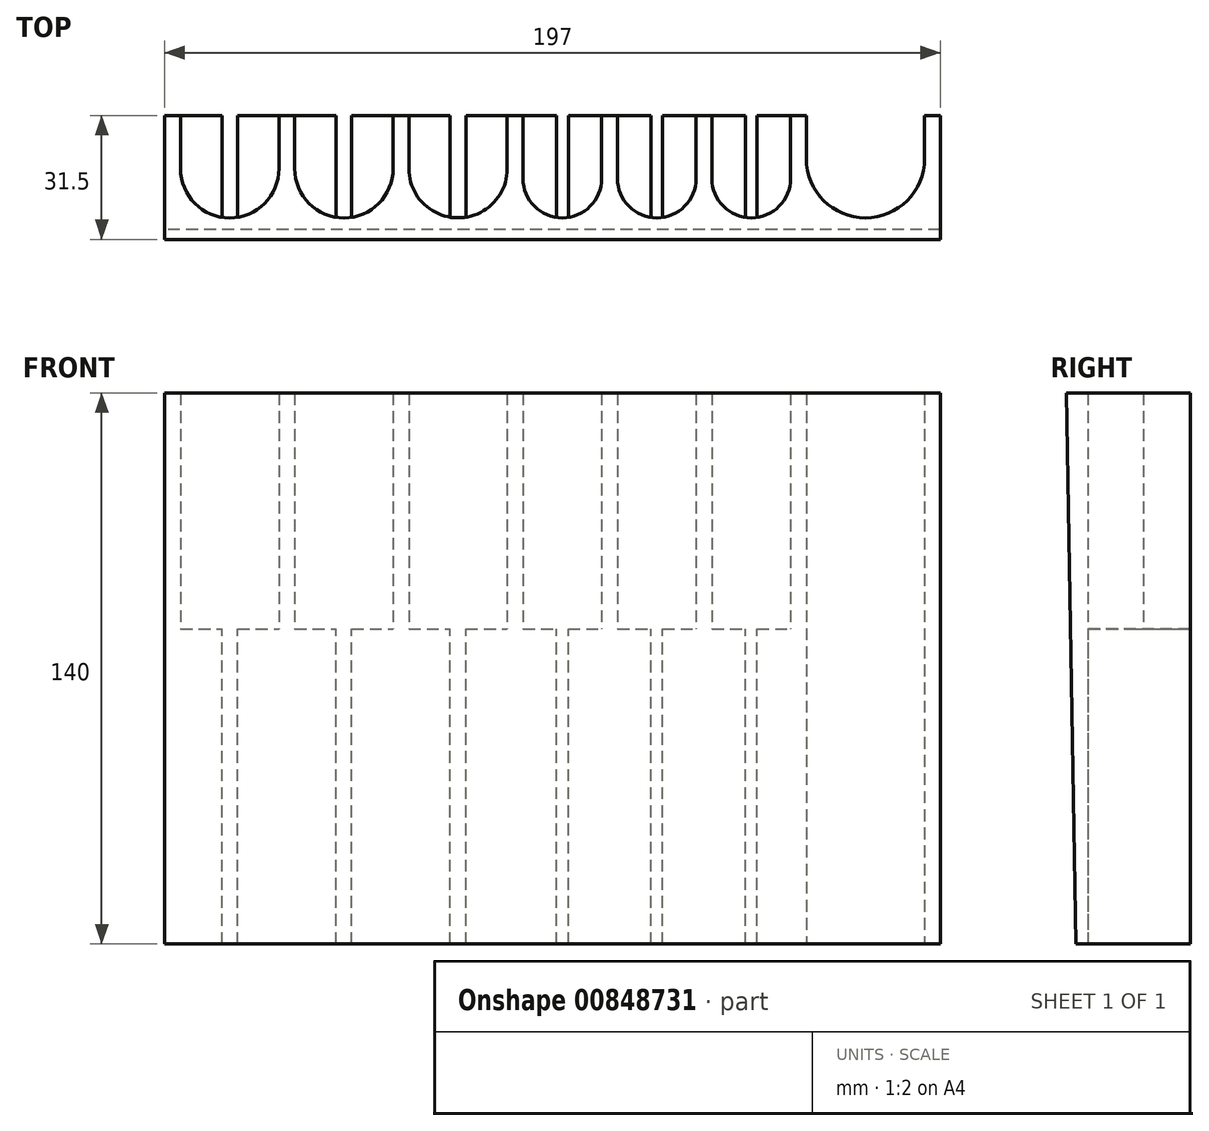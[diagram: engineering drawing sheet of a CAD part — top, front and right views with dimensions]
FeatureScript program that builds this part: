
annotation { "Feature Type Name" : "Feature", "Feature Type Description" : "" }
export const myFeature = defineFeature(function(context is Context, id is Id, definition is map)
    precondition{}
    {
        {
            var Q0;
            Q0=qCreatedBy(makeId("Top.planeOp"),FACE);
            var sketch = newSketch(context, id + "F0", { "sketchPlane" : qUnion([Q0])});
            skLineSegment(sketch, "E0.bottom", {"start": v(-180, 30) * mm, "end": v(0, 30) * mm});
            skLineSegment(sketch, "E0.top", {"start": v(-180, 0) * mm, "end": v(0, 0) * mm});
            skLineSegment(sketch, "E0.left", {"start": v(-180, 30) * mm, "end": v(-180, 0) * mm});
            skArc(sketch, "E1", {"start": v(-176, 16.5) * mm, "mid": v(-163.5, 4) * mm, "end": v(-151, 16.5) * mm});
            skArc(sketch, "E2", {"start": v(-147, 16.5) * mm, "mid": v(-134.5, 4) * mm, "end": v(-122, 16.5) * mm});
            skArc(sketch, "E3", {"start": v(-118, 16.5) * mm, "mid": v(-104.7, 4.03) * mm, "end": v(-93.1, 18.1) * mm});
            skArc(sketch, "E4", {"start": v(-89, 14) * mm, "mid": v(-79, 4) * mm, "end": v(-69, 14) * mm});
            skArc(sketch, "E5", {"start": v(-65, 14) * mm, "mid": v(-55, 4) * mm, "end": v(-45, 14) * mm});
            skArc(sketch, "E6", {"start": v(-41, 14) * mm, "mid": v(-31, 4) * mm, "end": v(-21, 14) * mm});
            skLineSegment(sketch, "E7.bottom", {"start": v(0, 30) * mm, "end": v(17, 30) * mm});
            skLineSegment(sketch, "E7.top", {"start": v(0, 0) * mm, "end": v(17, 0) * mm});
            skArc(sketch, "E8", {"start": v(-17, 19) * mm, "mid": v(-2, 4) * mm, "end": v(13, 19) * mm});
            skLineSegment(sketch, "E9", {"start": v(-176, 16.5) * mm, "end": v(-176, 30) * mm});
            skLineSegment(sketch, "E10", {"start": v(-151, 16.5) * mm, "end": v(-151, 30) * mm});
            skLineSegment(sketch, "E11", {"start": v(-147, 16.5) * mm, "end": v(-147, 30) * mm});
            skLineSegment(sketch, "E12", {"start": v(-122, 16.5) * mm, "end": v(-122, 30) * mm});
            skLineSegment(sketch, "E13", {"start": v(-118, 16.5) * mm, "end": v(-118, 30) * mm});
            skLineSegment(sketch, "E14", {"start": v(-93.1, 18.1) * mm, "end": v(-93.1, 30) * mm});
            skLineSegment(sketch, "E15", {"start": v(-89, 14) * mm, "end": v(-89, 30) * mm});
            skLineSegment(sketch, "E16", {"start": v(-69, 14) * mm, "end": v(-69, 30) * mm});
            skLineSegment(sketch, "E17", {"start": v(-65, 14) * mm, "end": v(-65, 30) * mm});
            skLineSegment(sketch, "E18", {"start": v(-45, 14) * mm, "end": v(-45, 30) * mm});
            skLineSegment(sketch, "E19", {"start": v(-41, 14) * mm, "end": v(-41, 30) * mm});
            skLineSegment(sketch, "E20", {"start": v(-21, 14) * mm, "end": v(-21, 30) * mm});
            skLineSegment(sketch, "E21", {"start": v(-17, 19) * mm, "end": v(-17, 30) * mm});
            skLineSegment(sketch, "E22", {"start": v(13, 19) * mm, "end": v(13, 30) * mm});
            skLineSegment(sketch, "E23", {"start": v(-56.5, 30) * mm, "end": v(-56.5, 10.18) * mm});
            skLineSegment(sketch, "E24", {"start": v(-53.5, 30) * mm, "end": v(-53.5, 10.01) * mm});
            skLineSegment(sketch, "E25", {"start": v(-32.5, 30) * mm, "end": v(-32.5, 17.37) * mm});
            skLineSegment(sketch, "E26", {"start": v(-29.5, 30) * mm, "end": v(-29.5, 17.22) * mm});
            skLineSegment(sketch, "E27", {"start": v(-80.5, 30) * mm, "end": v(-80.5, 18.02) * mm});
            skLineSegment(sketch, "E28", {"start": v(-77.5, 30) * mm, "end": v(-77.5, 17.52) * mm});
            skLineSegment(sketch, "E29", {"start": v(-132.5, 30) * mm, "end": v(-132.5, 14.05) * mm});
            skLineSegment(sketch, "E30", {"start": v(-136.5, 30) * mm, "end": v(-136.5, 13.27) * mm});
            skLineSegment(sketch, "E31", {"start": v(-161.5, 30) * mm, "end": v(-161.5, 11.13) * mm});
            skLineSegment(sketch, "E32", {"start": v(-165.5, 30) * mm, "end": v(-165.5, 8.65) * mm});
            skLineSegment(sketch, "E33", {"start": v(-107.5, 30) * mm, "end": v(-107.5, 11.19) * mm});
            skLineSegment(sketch, "E34", {"start": v(-103.5, 30) * mm, "end": v(-103.5, 10.64) * mm});
            skLineSegment(sketch, "E35", {"start": v(-165.5, 8.65) * mm, "end": v(-165.5, 4.16) * mm});
            skLineSegment(sketch, "E36", {"start": v(-161.5, 11.13) * mm, "end": v(-161.5, 4.16) * mm});
            skLineSegment(sketch, "E37", {"start": v(-136.5, 13.27) * mm, "end": v(-136.5, 4.16) * mm});
            skLineSegment(sketch, "E38", {"start": v(-132.5, 14.05) * mm, "end": v(-132.5, 4.16) * mm});
            skLineSegment(sketch, "E39", {"start": v(-107.5, 11.19) * mm, "end": v(-107.5, 4.16) * mm});
            skLineSegment(sketch, "E40", {"start": v(-103.5, 10.64) * mm, "end": v(-103.5, 4.16) * mm});
            skLineSegment(sketch, "E41", {"start": v(-80.5, 18.02) * mm, "end": v(-80.5, 4.11) * mm});
            skLineSegment(sketch, "E42", {"start": v(-77.5, 17.52) * mm, "end": v(-77.5, 4.11) * mm});
            skLineSegment(sketch, "E43", {"start": v(-56.5, 10.18) * mm, "end": v(-56.5, 4.11) * mm});
            skLineSegment(sketch, "E44", {"start": v(-53.5, 10.01) * mm, "end": v(-53.5, 4.11) * mm});
            skLineSegment(sketch, "E45", {"start": v(-32.5, 17.37) * mm, "end": v(-32.5, 4.11) * mm});
            skLineSegment(sketch, "E46", {"start": v(-29.5, 17.22) * mm, "end": v(-29.5, 4.11) * mm});
            skLineSegment(sketch, "E47", {"start": v(17, 30) * mm, "end": v(17, 0) * mm});
            skPoint(sketch, "E48.orphan", {"position": v(20, 0) * mm});
            skSolve(sketch);
        }
        {
            var Q0;
            Q0=makeQuery(id+"F0.imprint","IMPRINT",FACE,{"disambiguationData":[TD([[makeQuery(id+"F0.imprint","IMPRINT",EDGE,{"derivedFrom":sQuery(id+"F0.wireOp",EDGE,"E0.top")}),1.0]])]});
            extrude(context, id + "F1", {"entities" : qUnion([Q0]), "depth" : 60 * mm, "offsetDistance" : 25 * mm});
        }
        {
            var Q0;
            Q0=makeQuery(id+"F0.imprint","IMPRINT",FACE,{"disambiguationData":[TD([[makeQuery(id+"F0.imprint","IMPRINT",EDGE,{"derivedFrom":sQuery(id+"F0.wireOp",EDGE,"E0.top")}),1.0]])]});
            var Q1;
            {var subQ1=sQuery(id+"F0.wireOp",EDGE,"E9");Q1=makeQuery(id+"F0.imprint","IMPRINT",FACE,{"disambiguationData":[TD([[makeQuery(id+"F0.imprint","IMPRINT",EDGE,{"derivedFrom":subQ1}),-1.0]])]});}
            var Q2;
            {var subQ0=sQuery(id+"F0.wireOp",EDGE,"E10");Q2=makeQuery(id+"F0.imprint","IMPRINT",FACE,{"disambiguationData":[TD([[makeQuery(id+"F0.imprint","IMPRINT",EDGE,{"derivedFrom":subQ0}),1.0]])]});}
            var Q3;
            {var subQ1=sQuery(id+"F0.wireOp",EDGE,"E11");Q3=makeQuery(id+"F0.imprint","IMPRINT",FACE,{"disambiguationData":[TD([[makeQuery(id+"F0.imprint","IMPRINT",EDGE,{"derivedFrom":subQ1}),-1.0]])]});}
            var Q4;
            {var subQ1=sQuery(id+"F0.wireOp",EDGE,"E12");Q4=makeQuery(id+"F0.imprint","IMPRINT",FACE,{"disambiguationData":[TD([[makeQuery(id+"F0.imprint","IMPRINT",EDGE,{"derivedFrom":subQ1}),1.0]])]});}
            var Q5;
            {var subQ1=sQuery(id+"F0.wireOp",EDGE,"E13");Q5=makeQuery(id+"F0.imprint","IMPRINT",FACE,{"disambiguationData":[TD([[makeQuery(id+"F0.imprint","IMPRINT",EDGE,{"derivedFrom":subQ1}),-1.0]])]});}
            var Q6;
            {var subQ1=sQuery(id+"F0.wireOp",EDGE,"E14");Q6=makeQuery(id+"F0.imprint","IMPRINT",FACE,{"disambiguationData":[TD([[makeQuery(id+"F0.imprint","IMPRINT",EDGE,{"derivedFrom":subQ1}),1.0]])]});}
            var Q7;
            {var subQ1=sQuery(id+"F0.wireOp",EDGE,"E15");Q7=makeQuery(id+"F0.imprint","IMPRINT",FACE,{"disambiguationData":[TD([[makeQuery(id+"F0.imprint","IMPRINT",EDGE,{"derivedFrom":subQ1}),-1.0]])]});}
            var Q8;
            {var subQ0=sQuery(id+"F0.wireOp",EDGE,"E16");Q8=makeQuery(id+"F0.imprint","IMPRINT",FACE,{"disambiguationData":[TD([[makeQuery(id+"F0.imprint","IMPRINT",EDGE,{"derivedFrom":subQ0}),1.0]])]});}
            var Q9;
            {var subQ0=sQuery(id+"F0.wireOp",EDGE,"E17");Q9=makeQuery(id+"F0.imprint","IMPRINT",FACE,{"disambiguationData":[TD([[makeQuery(id+"F0.imprint","IMPRINT",EDGE,{"derivedFrom":subQ0}),-1.0]])]});}
            var Q10;
            {var subQ1=sQuery(id+"F0.wireOp",EDGE,"E18");Q10=makeQuery(id+"F0.imprint","IMPRINT",FACE,{"disambiguationData":[TD([[makeQuery(id+"F0.imprint","IMPRINT",EDGE,{"derivedFrom":subQ1}),1.0]])]});}
            var Q11;
            {var subQ1=sQuery(id+"F0.wireOp",EDGE,"E19");Q11=makeQuery(id+"F0.imprint","IMPRINT",FACE,{"disambiguationData":[TD([[makeQuery(id+"F0.imprint","IMPRINT",EDGE,{"derivedFrom":subQ1}),-1.0]])]});}
            var Q12;
            {var subQ0=sQuery(id+"F0.wireOp",EDGE,"E20");Q12=makeQuery(id+"F0.imprint","IMPRINT",FACE,{"disambiguationData":[TD([[makeQuery(id+"F0.imprint","IMPRINT",EDGE,{"derivedFrom":subQ0}),1.0]])]});}
            extrude(context, id + "F2", {"entities" : qUnion([Q0, Q1, Q2, Q3, Q4, Q5, Q6, Q7, Q8, Q9, Q10, Q11, Q12]), "operationType" : NewBodyOperationType.ADD, "oppositeDirection" : true, "depth" : 80 * mm, "offsetDistance" : 25 * mm});
        }
        {
            var Q0;
            {var subQ0=sQuery(id+"F0.wireOp",EDGE,"E0.left");Q0=makeQuery(id+"F2.boolean.opBoolean","MERGE",FACE,{"derivedFrom":[makeQuery(id+"F1.opExtrude","SWEPT_FACE",FACE,{"disambiguationData":[OSD([subQ0])]}),makeQuery(id+"F2.opExtrude","SWEPT_FACE",FACE,{"disambiguationData":[OSD([subQ0])]})]});}
            var sketch = newSketch(context, id + "F3", { "sketchPlane" : qUnion([Q0])});
            skLineSegment(sketch, "E49", {"start": v(1.5, 60) * mm, "end": v(0, 60) * mm});
            skLineSegment(sketch, "E50", {"start": v(0, 60) * mm, "end": v(0, -80) * mm});
            skLineSegment(sketch, "E51", {"start": v(1.5, 60) * mm, "end": v(-1, -80) * mm});
            skLineSegment(sketch, "E52", {"start": v(-1, -80) * mm, "end": v(0, -80) * mm});
            skSolve(sketch);
        }
        {
            var Q0;
            {var subQ0=sQuery(id+"F3.wireOp",EDGE,"E49");Q0=makeQuery(id+"F3.imprint","IMPRINT",FACE,{"disambiguationData":[TD([[makeQuery(id+"F3.imprint","IMPRINT",EDGE,{"derivedFrom":subQ0}),1.0]])]});}
            var Q1;
            {var subQ0=sQuery(id+"F0.wireOp",EDGE,"E47");Q1=makeQuery(id+"F2.boolean.opBoolean","MERGE",FACE,{"derivedFrom":[makeQuery(id+"F1.opExtrude","SWEPT_FACE",FACE,{"disambiguationData":[OSD([subQ0])]}),makeQuery(id+"F2.opExtrude","SWEPT_FACE",FACE,{"disambiguationData":[OSD([subQ0])]})]});}
            extrude(context, id + "F4", {"entities" : qUnion([Q0]), "operationType" : NewBodyOperationType.ADD, "endBound" : BoundingType.UP_TO_SURFACE, "oppositeDirection" : true, "depth" : 25 * mm, "endBoundEntityFace" : qUnion([Q1]), "offsetDistance" : 25 * mm});
        }
        {
            var Q0;
            {var subQ0=sQuery(id+"F3.wireOp",EDGE,"E52");Q0=makeQuery(id+"F3.imprint","IMPRINT",FACE,{"disambiguationData":[TD([[makeQuery(id+"F3.imprint","IMPRINT",EDGE,{"derivedFrom":subQ0}),1.0]])]});}
            var Q1;
            {var subQ0=sQuery(id+"F0.wireOp",EDGE,"E47");Q1=makeQuery(id+"F4.boolean.opBoolean","MERGE",FACE,{"derivedFrom":[makeQuery(id+"F2.boolean.opBoolean","MERGE",FACE,{"derivedFrom":[makeQuery(id+"F1.opExtrude","SWEPT_FACE",FACE,{"disambiguationData":[OSD([subQ0])]}),makeQuery(id+"F2.opExtrude","SWEPT_FACE",FACE,{"disambiguationData":[OSD([subQ0])]})]}),makeQuery(id+"F4.opExtrude","CAP_FACE",FACE,{"disambiguationData":[OSD([subQ0])],"isStart":false})]});}
            extrude(context, id + "F5", {"entities" : qUnion([Q0]), "operationType" : NewBodyOperationType.REMOVE, "endBound" : BoundingType.UP_TO_SURFACE, "oppositeDirection" : true, "depth" : 25 * mm, "endBoundEntityFace" : qUnion([Q1]), "offsetDistance" : 25 * mm});
        }
    });
